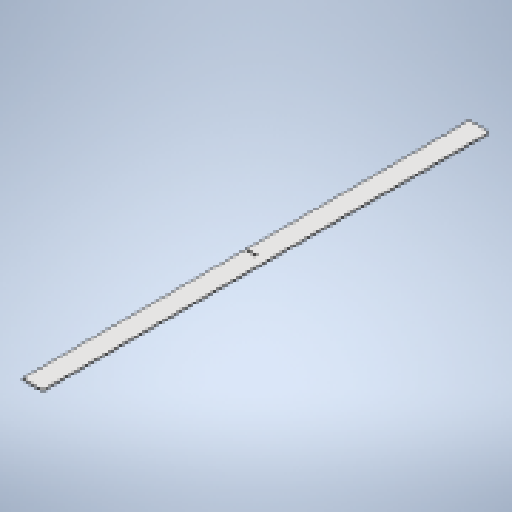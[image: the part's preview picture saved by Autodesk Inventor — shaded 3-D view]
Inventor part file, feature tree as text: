
AUTODESK INVENTOR PART (.ipt)
format: ipt  version: 2025 (Build 290162010, 162A)  size: 160,256 bytes
history: native  units: mm
features: sheet_metal_op x1, chamfer x1, sketch x1, other x1
ambient origin geometry x8: Origin, YZ Plane, XZ Plane, XY Plane, X Axis, Y Axis, Z Axis, Center Point
bodies: Body1 (feature_tree)
feature tree (4):
  sheet_metal_op  "Face2"
  chamfer  "Corner Round2"
  sketch  "Sketch1"  dims[d15=3.0mm d17=1098.0mm d18=50.0mm d19=3.0mm d20=26.0mm d22=6.0mm]
  other  "Plate2"
